# Revit family: Haworth_XSeries_RecycleStation
name_source: partatom
category: Furniture Systems
units: mm (PartAtom-declared; Revit-internal decimal feet)

## family parameters
Always vertical = Yes
Cut with Voids When Loaded = No
OmniClass Number = 23.40.70.14.64.21
OmniClass Title = Systems Furniture
Part Type = Normal
Room Calculation Point = No
Round Connector Dimension = Use Diameter
Shared = No
Work Plane-Based = No

## types (1)
- 18d 48w 39h
    Actual Depth = 18 3/4"
    Actual Height = 39 1/2"
    Actual Width = 48"
    Assembly Code = E2020200
    Base Height = 1 7/8"
    Description = Haworth XSeries Recycle Station - 18d 48w 39h
    Door Height = 35 3/4"
    Door Offset = 1/16"
    Manufacturer = Haworth
    Model = JRPY-3948-SJAN
    Opening Radius = 2 1/2"
    Opening Spacing = 14"
    Overlay Finish = Haworth _ Acrylic _ White
    Overlay Height = 1/2"
    Panel Thickness = 3/4"
    Revision Number = 3
    Size = Verify Final Dim. w/ Haworth
    Standard Depths = 18.75 in.
    Standard Heights = 39.5 in.
    Standard Widths = 48 in.
    Sustainability Info = https://www.haworth.com
    Top Height = 1 1/4"
    URL = http://www.haworth.com
    URL - Product = https://www.haworth.com
    Warranty = https://cdn.shopify.com

## geometry (parser evidence)
native form markers: Sweep x6
no freeform markers — native parametric forms only
